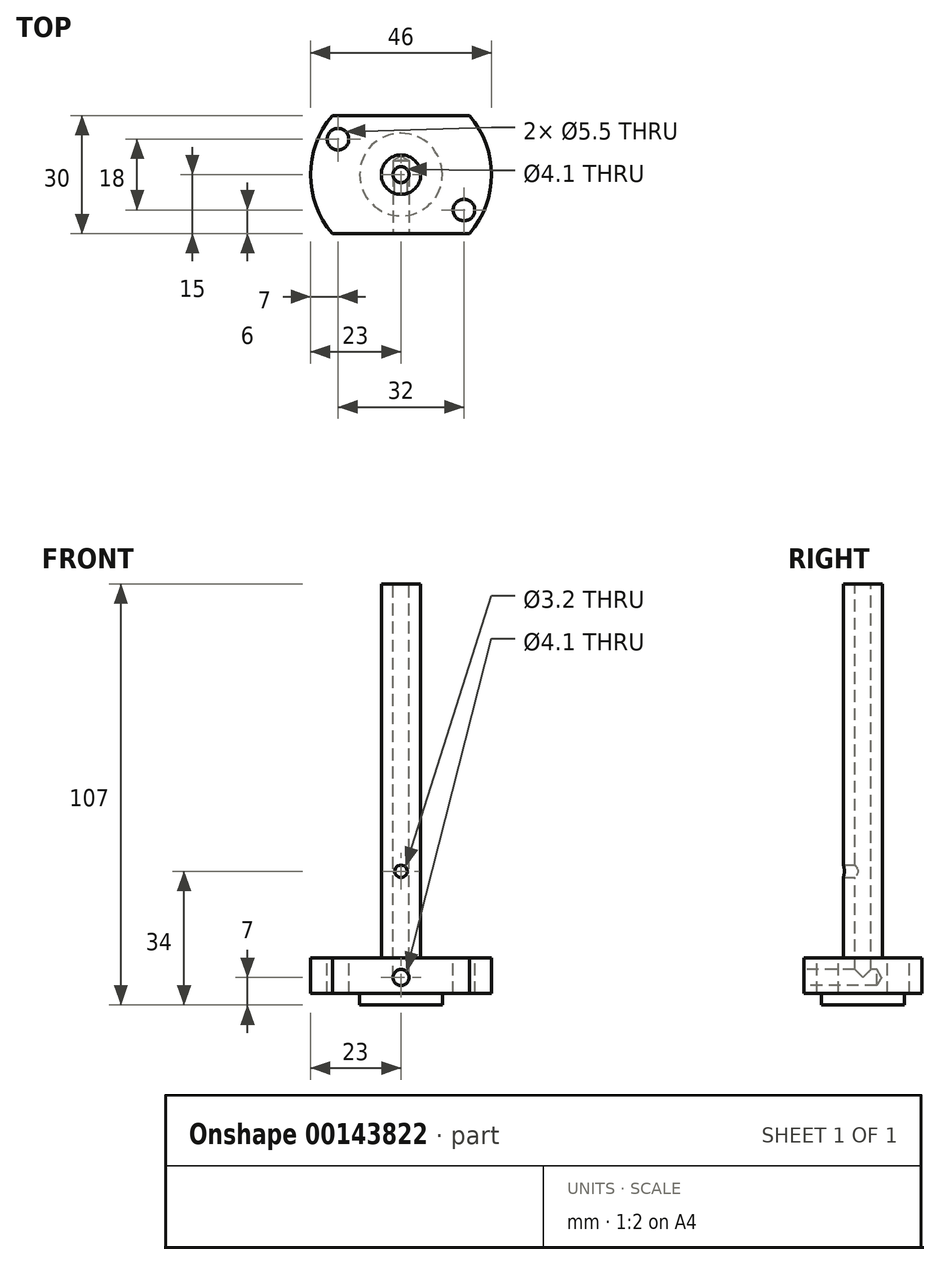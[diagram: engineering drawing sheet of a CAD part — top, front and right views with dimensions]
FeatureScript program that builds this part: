
annotation { "Feature Type Name" : "Feature", "Feature Type Description" : "" }
export const myFeature = defineFeature(function(context is Context, id is Id, definition is map)
    precondition{}
    {
        {
            var Q0;
            Q0=qCreatedBy(makeId("Top.planeOp"),FACE);
            var sketch = newSketch(context, id + "F0", { "sketchPlane" : qUnion([Q0])});
            skArc(sketch, "E0", {"start": v(-17.44, 15) * mm, "mid": v(-23, 0) * mm, "end": v(-17.44, -15) * mm});
            skLineSegment(sketch, "E1", {"start": v(-17.44, -15) * mm, "end": v(17.44, -15) * mm});
            skLineSegment(sketch, "E2", {"start": v(-17.44, 15) * mm, "end": v(17.44, 15) * mm});
            skLineSegment(sketch, "E3", {"start": v(-17.43, -15) * mm, "end": v(-17.43, -15) * mm});
            skLineSegment(sketch, "E4", {"start": v(17.44, -15) * mm, "end": v(17.44, -15) * mm});
            skArc(sketch, "E5.trimOffspring", {"start": v(17.43, -15) * mm, "mid": v(23, 0) * mm, "end": v(17.43, 15) * mm});
            skLineSegment(sketch, "E6.trimOffspring", {"start": v(-17.43, 15) * mm, "end": v(-17.43, 15) * mm});
            skLineSegment(sketch, "E7.trimOffspring", {"start": v(17.43, 15) * mm, "end": v(17.43, 15) * mm});
            skSolve(sketch);
        }
        {
            var Q0;
            {var subQ1=sQuery(id+"F0.wireOp",EDGE,"E1");var subQ7=sQuery(id+"F0.wireOp",EDGE,"E0");var subQ8=makeQuery(id+"F0.imprint","INTERSECT",VERTEX,{"derivedFrom":[subQ7,subQ1]});Q0=makeQuery(id+"F0.imprint","IMPRINT",FACE,{"disambiguationData":[TD([[makeQuery(id+"F0.imprint","IMPRINT",EDGE,{"disambiguationData":[TD([[subQ8,1.0]])],"derivedFrom":subQ7}),1.0]])]});}
            extrude(context, id + "F1", {"entities" : qUnion([Q0]), "depth" : 9 * mm});
        }
        {
            var Q0;
            Q0=makeQuery(id+"F1.opExtrude","CAP_FACE",FACE,{"disambiguationData":[OSD([sQuery(id+"F0.wireOp",EDGE,"E0"),sQuery(id+"F0.wireOp",EDGE,"E1"),sQuery(id+"F0.wireOp",EDGE,"E2"),sQuery(id+"F0.wireOp",EDGE,"E5.trimOffspring")])],"isStart":true});
            var sketch = newSketch(context, id + "F2", { "sketchPlane" : qUnion([Q0])});
            skCircle(sketch, "E8", {"center": v(0, 0) * mm, "radius": 10.5 * mm});
            skSolve(sketch);
        }
        {
            var Q0;
            Q0=makeQuery(id+"F2.imprint","IMPRINT",FACE,{"disambiguationData":[TD([[makeQuery(id+"F2.imprint","IMPRINT",EDGE,{"derivedFrom":sQuery(id+"F2.wireOp",EDGE,"E8")}),1.0]])]});
            extrude(context, id + "F3", {"entities" : qUnion([Q0]), "operationType" : NewBodyOperationType.ADD, "depth" : 3 * mm});
        }
        {
            var Q0;
            Q0=makeQuery(id+"F1.opExtrude","CAP_FACE",FACE,{"disambiguationData":[OSD([sQuery(id+"F0.wireOp",EDGE,"E0"),sQuery(id+"F0.wireOp",EDGE,"E1"),sQuery(id+"F0.wireOp",EDGE,"E2"),sQuery(id+"F0.wireOp",EDGE,"E5.trimOffspring")])],"isStart":false});
            var sketch = newSketch(context, id + "F4", { "sketchPlane" : qUnion([Q0])});
            skCircle(sketch, "E9", {"center": v(0, 0) * mm, "radius": 5 * mm});
            skSolve(sketch);
        }
        {
            var Q0;
            Q0=makeQuery(id+"F4.imprint","IMPRINT",FACE,{"disambiguationData":[TD([[makeQuery(id+"F4.imprint","IMPRINT",EDGE,{"derivedFrom":sQuery(id+"F4.wireOp",EDGE,"E9")}),1.0]])]});
            extrude(context, id + "F5", {"entities" : qUnion([Q0]), "operationType" : NewBodyOperationType.ADD, "depth" : 95 * mm});
        }
        {
            var Q0;
            Q0=qCreatedBy(makeId("Front.planeOp"),FACE);
            var sketch = newSketch(context, id + "F6", { "sketchPlane" : qUnion([Q0])});
            skCircle(sketch, "E10", {"center": v(0, 31) * mm, "radius": 1.6 * mm});
            skSolve(sketch);
        }
        {
            var Q0;
            Q0=sQuery(id+"F6.wireOp",VERTEX,"E10.center");
            var Q1;
            Q1=makeQuery(id+"F1.opExtrude","SWEPT_BODY",BODY,{"disambiguationData":[OSD([sQuery(id+"F0.wireOp",EDGE,"E0"),sQuery(id+"F0.wireOp",EDGE,"E1"),sQuery(id+"F0.wireOp",EDGE,"E2"),sQuery(id+"F0.wireOp",EDGE,"E5.trimOffspring")])]});
            hole(context, id + "F7", {"style" : HoleStyle.SIMPLE, "endStyle" : HoleEndStyle.BLIND, "oppositeDirection" : true, "standardTappedOrClearance" : lookupTablePath({ "standard" : "ISO", "engagement" : "75%", "pitch" : "0.75 mm", "size" : "M4", "type" : "Tapped" }), "standardBlindInLast" : lookupTablePath({ "standard" : "ISO", "engagement" : "75%", "pitch" : "0.75 mm", "size" : "M4", "type" : "Tapped" }), "holeDiameter" : 3.2 * mm, "holeDepth" : 5 * mm, "startFromSketch" : true, "locations" : qUnion([Q0]), "scope" : qUnion([Q1])});
        }
        {
            var Q0;
            Q0=makeQuery(id+"F1.opExtrude","SWEPT_FACE",FACE,{"disambiguationData":[OSD([sQuery(id+"F0.wireOp",EDGE,"E1")])]});
            var sketch = newSketch(context, id + "F8", { "sketchPlane" : qUnion([Q0])});
            skCircle(sketch, "E11", {"center": v(0, 4) * mm, "radius": 2.07 * mm});
            skSolve(sketch);
        }
        {
            var Q0;
            Q0=sQuery(id+"F8.wireOp",VERTEX,"E11.center");
            var Q1;
            Q1=makeQuery(id+"F1.opExtrude","SWEPT_BODY",BODY,{"disambiguationData":[OSD([sQuery(id+"F0.wireOp",EDGE,"E0"),sQuery(id+"F0.wireOp",EDGE,"E1"),sQuery(id+"F0.wireOp",EDGE,"E2"),sQuery(id+"F0.wireOp",EDGE,"E5.trimOffspring")])]});
            hole(context, id + "F9", {"style" : HoleStyle.SIMPLE, "endStyle" : HoleEndStyle.BLIND, "standardTappedOrClearance" : lookupTablePath({ "standard" : "ISO", "engagement" : "75%", "pitch" : "0.9 mm", "size" : "M5", "type" : "Tapped" }), "standardBlindInLast" : lookupTablePath({ "standard" : "ISO", "engagement" : "75%", "pitch" : "0.9 mm", "size" : "M5", "type" : "Tapped" }), "holeDiameter" : 4.1 * mm, "holeDepth" : 18.5 * mm, "startFromSketch" : true, "locations" : qUnion([Q0]), "scope" : qUnion([Q1])});
        }
        {
            var Q0;
            Q0=makeQuery(id+"F5.opExtrude","CAP_FACE",FACE,{"disambiguationData":[OSD([sQuery(id+"F4.wireOp",EDGE,"E9")])],"isStart":false});
            var sketch = newSketch(context, id + "F10", { "sketchPlane" : qUnion([Q0])});
            skCircle(sketch, "E12", {"center": v(0, 0) * mm, "radius": 1.6 * mm});
            skSolve(sketch);
        }
        {
            var Q0;
            Q0=sQuery(id+"F10.wireOp",VERTEX,"E12.center");
            var Q1;
            Q1=makeQuery(id+"F1.opExtrude","SWEPT_BODY",BODY,{"disambiguationData":[OSD([sQuery(id+"F0.wireOp",EDGE,"E0"),sQuery(id+"F0.wireOp",EDGE,"E1"),sQuery(id+"F0.wireOp",EDGE,"E2"),sQuery(id+"F0.wireOp",EDGE,"E5.trimOffspring")])]});
            hole(context, id + "F11", {"style" : HoleStyle.SIMPLE, "endStyle" : HoleEndStyle.BLIND, "standardTappedOrClearance" : lookupTablePath({ "standard" : "ISO", "engagement" : "75%", "pitch" : "0.9 mm", "size" : "M5", "type" : "Tapped" }), "standardBlindInLast" : lookupTablePath({ "standard" : "ISO", "engagement" : "75%", "pitch" : "0.9 mm", "size" : "M5", "type" : "Tapped" }), "holeDiameter" : 4.1 * mm, "holeDepth" : 100 * mm, "startFromSketch" : true, "locations" : qUnion([Q0]), "scope" : qUnion([Q1])});
        }
        {
            var Q0;
            Q0=makeQuery(id+"F1.opExtrude","CAP_FACE",FACE,{"disambiguationData":[OSD([sQuery(id+"F0.wireOp",EDGE,"E0"),sQuery(id+"F0.wireOp",EDGE,"E1"),sQuery(id+"F0.wireOp",EDGE,"E2"),sQuery(id+"F0.wireOp",EDGE,"E5.trimOffspring")])],"isStart":false});
            var sketch = newSketch(context, id + "F12", { "sketchPlane" : qUnion([Q0])});
            skCircle(sketch, "E13", {"center": v(-16, 9) * mm, "radius": 2.75 * mm});
            skCircle(sketch, "E14", {"center": v(16, -9) * mm, "radius": 2.75 * mm});
            skSolve(sketch);
        }
        {
            var Q0;
            Q0=sQuery(id+"F12.wireOp",VERTEX,"E13.center");
            var Q1;
            Q1=sQuery(id+"F12.wireOp",VERTEX,"E14.center");
            var Q2;
            Q2=makeQuery(id+"F1.opExtrude","SWEPT_BODY",BODY,{"disambiguationData":[OSD([sQuery(id+"F0.wireOp",EDGE,"E0"),sQuery(id+"F0.wireOp",EDGE,"E1"),sQuery(id+"F0.wireOp",EDGE,"E2"),sQuery(id+"F0.wireOp",EDGE,"E5.trimOffspring")])]});
            hole(context, id + "F13", {"style" : HoleStyle.SIMPLE, "endStyle" : HoleEndStyle.BLIND, "standardTappedOrClearance" : lookupTablePath({ "standard" : "ISO", "fit" : "Normal", "size" : "M5", "type" : "Clearance" }), "standardBlindInLast" : lookupTablePath({ "fit" : "Standard", "standard" : "ISO", "size" : "M5", "type" : "Clearance" }), "holeDiameter" : 5.5 * mm, "holeDepth" : 9 * mm, "startFromSketch" : true, "locations" : qUnion([Q0, Q1]), "scope" : qUnion([Q2])});
        }
    });
